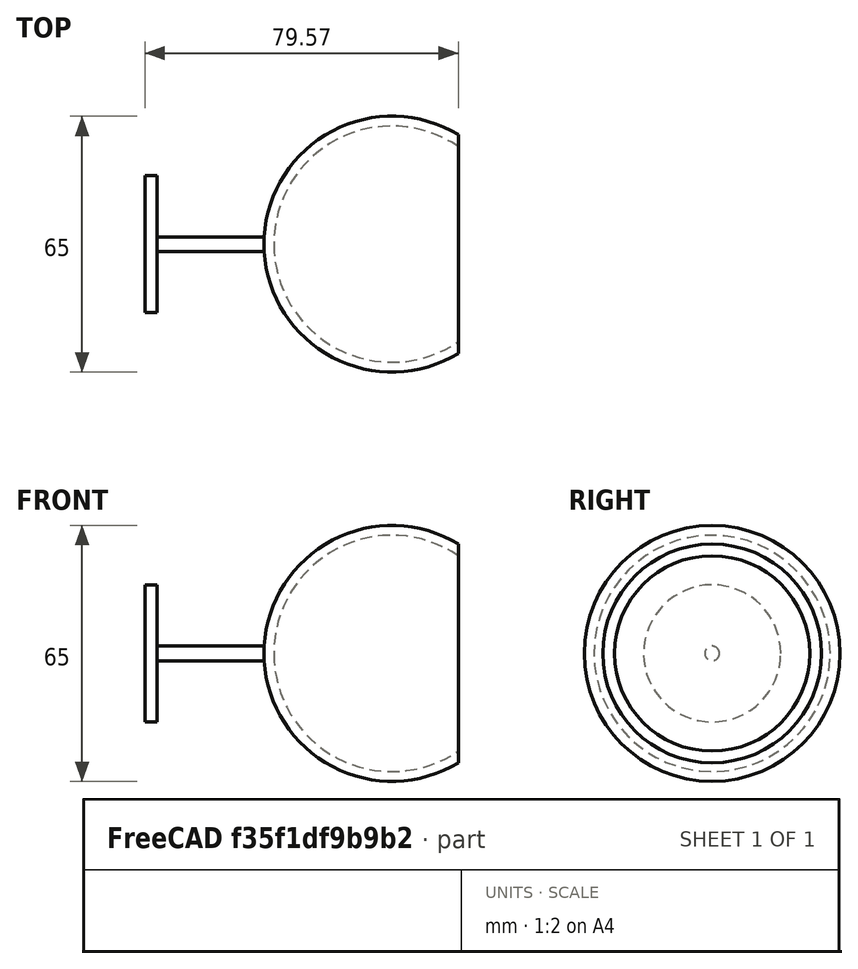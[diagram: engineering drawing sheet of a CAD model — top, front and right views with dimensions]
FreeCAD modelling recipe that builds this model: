
FCSTD DOCUMENT  (FreeCAD 0.19R24276 (Git))
Label: bokal_v1_1
License: All rights reserved
LicenseURL: http://en.wikipedia.org/wiki/All_rights_reserved
objects: Sketcher::SketchObject×1, PartDesign::Revolution×1, PartDesign::Body×1
note: 4 computed .brp shape members not serialized (recipe doc carries the construction recipe); baked Part::Feature solids carry a one-line shape summary decoded from their .brp

FEATURE [Sketcher::SketchObject] Sketch
  FullyConstrained = false
  MapMode = 5
  Support = -> [XY_Plane]
  sketch-geometry (8):
    g0: ArcOfCircle CenterX=0 CenterY=0 CenterZ=0 NormalX=0 NormalY=0 NormalZ=1 AngleXU=0 Radius=32.5 StartAngle=1.02524 EndAngle=3.08464
    g1: ArcOfCircle CenterX=0 CenterY=0 CenterZ=0 NormalX=0 NormalY=0 NormalZ=1 AngleXU=0 Radius=30 StartAngle=0.973837 EndAngle=3.14159
    g2: LineSegment StartX=16.8639 StartY=24.8115 StartZ=0 EndX=16.8639 EndY=27.7823 EndZ=0
    g3: LineSegment StartX=-30 StartY=3.7e-15 StartZ=0 EndX=-62.7076 EndY=3.1e-15 EndZ=0
    g4: LineSegment StartX=-59.7076 StartY=17.4251 StartZ=0 EndX=-62.7076 EndY=17.4251 EndZ=0
    g5: LineSegment StartX=-62.7076 StartY=17.4251 StartZ=0 EndX=-62.7076 EndY=3.6e-15 EndZ=0
    g6: LineSegment StartX=-59.7076 StartY=1.84983 StartZ=0 EndX=-59.7076 EndY=17.4251 EndZ=0
    g7: LineSegment StartX=-59.7076 StartY=1.84983 StartZ=0 EndX=-32.4473 EndY=1.84983 EndZ=0
  constraints (15):
    c: Coincident(g0,g-1)
    c: Coincident(g1,g0)
    c: Coincident(g2,g1)
    c: PointOnObject(g2,g0)
    c: Coincident(g4,g5)
    c: Coincident(g6,g4)
    c: Horizontal(g4)
    c: Vertical(g5)
    c: Vertical(g6)
    c: DistanceX(g4,g4) = 3
    c: Coincident(g3,g5)
    c: Horizontal(g7)
    c: Coincident(g6,g7)
    c: Coincident(g0,g7)
    c: Coincident(g3,g1)
FEATURE [PartDesign::Revolution] Revolution
  Angle = 360
  Axis = (1,0,0)
  Base = (0,0,0)
  Profile = -> Sketch
  ReferenceAxis = -> Sketch [H_Axis]
FEATURE [PartDesign::Body] Body
  Group = -> [Sketch,Revolution]
  Origin = -> Origin
  Tip = -> Revolution
